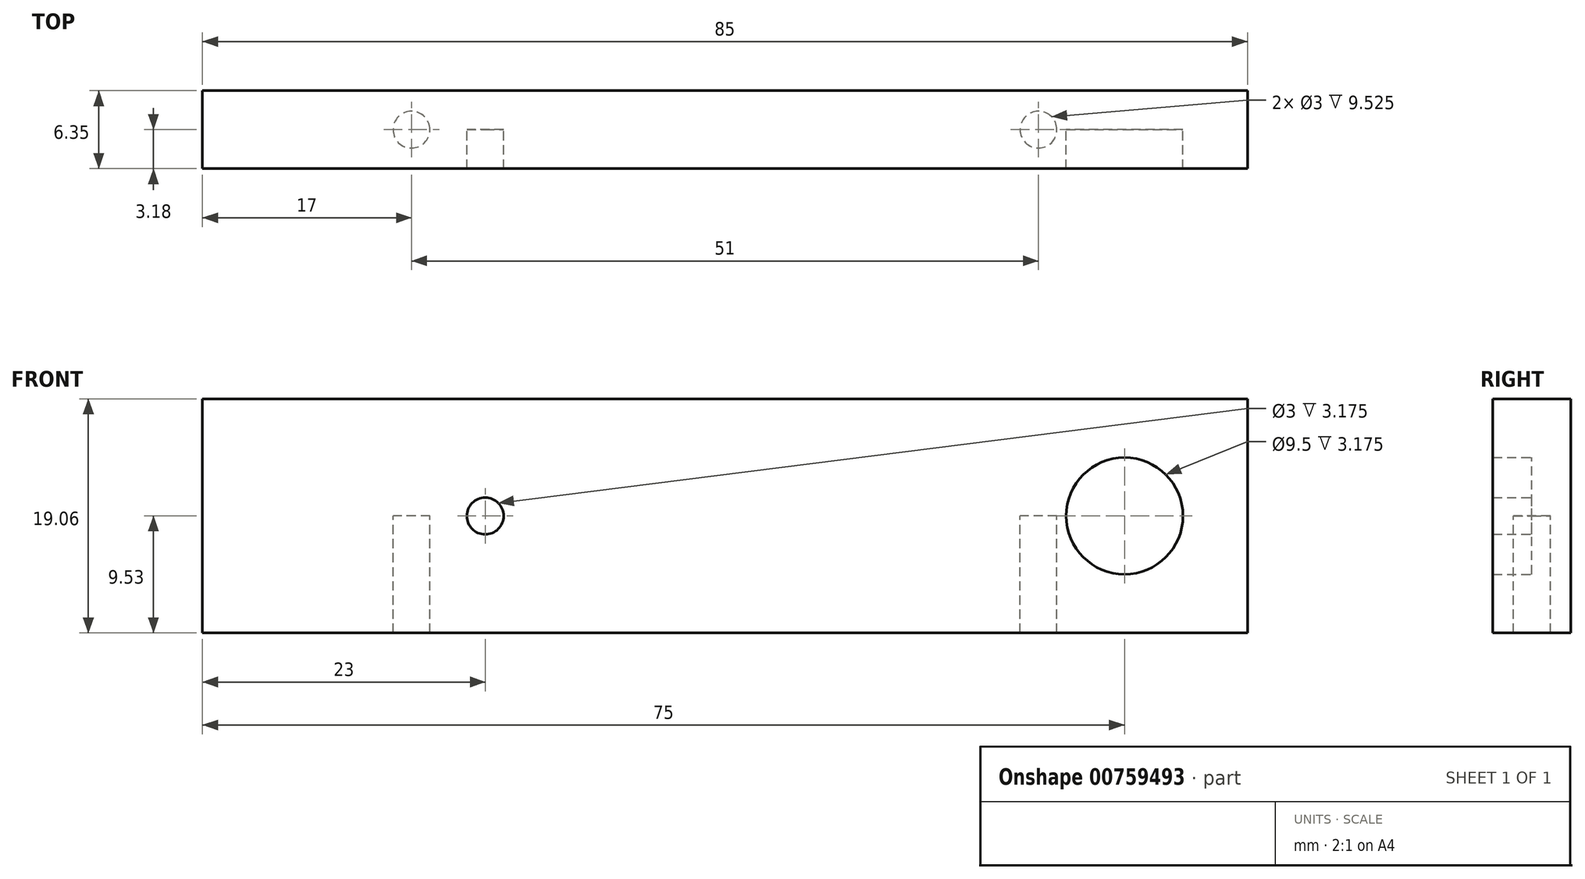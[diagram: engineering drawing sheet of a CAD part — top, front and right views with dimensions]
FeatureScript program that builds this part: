
annotation { "Feature Type Name" : "Feature", "Feature Type Description" : "" }
export const myFeature = defineFeature(function(context is Context, id is Id, definition is map)
    precondition{}
    {
        {
            var Q0;
            Q0=qCreatedBy(makeId("Front.planeOp"),FACE);
            var sketch = newSketch(context, id + "F0", { "sketchPlane" : qUnion([Q0])});
            skLineSegment(sketch, "E0.bottom", {"start": v(-42.5, 9.52) * mm, "end": v(42.5, 9.52) * mm});
            skLineSegment(sketch, "E0.top", {"start": v(-42.5, -9.52) * mm, "end": v(42.5, -9.52) * mm});
            skLineSegment(sketch, "E0.left", {"start": v(-42.5, 9.52) * mm, "end": v(-42.5, -9.52) * mm});
            skLineSegment(sketch, "E0.right", {"start": v(42.5, 9.52) * mm, "end": v(42.5, -9.52) * mm});
            skPoint(sketch, "E0.middle", {"position": v(0, 0) * mm});
            skSolve(sketch);
        }
        {
            var Q0;
            Q0 = qSketchRegion(id + "F0", true);
            extrude(context, id + "F1", {"entities" : qUnion([Q0]), "endBound" : BoundingType.SYMMETRIC, "depth" : 6.35 * mm, "offsetDistance" : 25 * mm});
        }
        {
            var Q0;
            Q0=qCreatedBy(makeId("Top.planeOp"),FACE);
            var sketch = newSketch(context, id + "F2", { "sketchPlane" : qUnion([Q0])});
            skCircle(sketch, "E1", {"center": v(-25.5, 0) * mm, "radius": 1.5 * mm});
            skCircle(sketch, "E2", {"center": v(25.5, 0) * mm, "radius": 1.5 * mm});
            skSolve(sketch);
        }
        {
            var Q0;
            Q0=qCreatedBy(makeId("Front.planeOp"),FACE);
            var sketch = newSketch(context, id + "F3", { "sketchPlane" : qUnion([Q0])});
            skCircle(sketch, "E3", {"center": v(32.5, 0) * mm, "radius": 4.75 * mm});
            skCircle(sketch, "E4", {"center": v(-19.5, 0) * mm, "radius": 1.5 * mm});
            skSolve(sketch);
        }
        {
            var Q0;
            Q0 = qSketchRegion(id + "F3", true);
            extrude(context, id + "F4", {"entities" : qUnion([Q0]), "operationType" : NewBodyOperationType.REMOVE, "depth" : 21.8 * mm, "offsetDistance" : 25 * mm});
        }
        {
            var Q0;
            Q0 = qSketchRegion(id + "F2", true);
            extrude(context, id + "F5", {"entities" : qUnion([Q0]), "operationType" : NewBodyOperationType.REMOVE, "oppositeDirection" : true, "depth" : 15 * mm, "offsetDistance" : 25 * mm});
        }
    });
